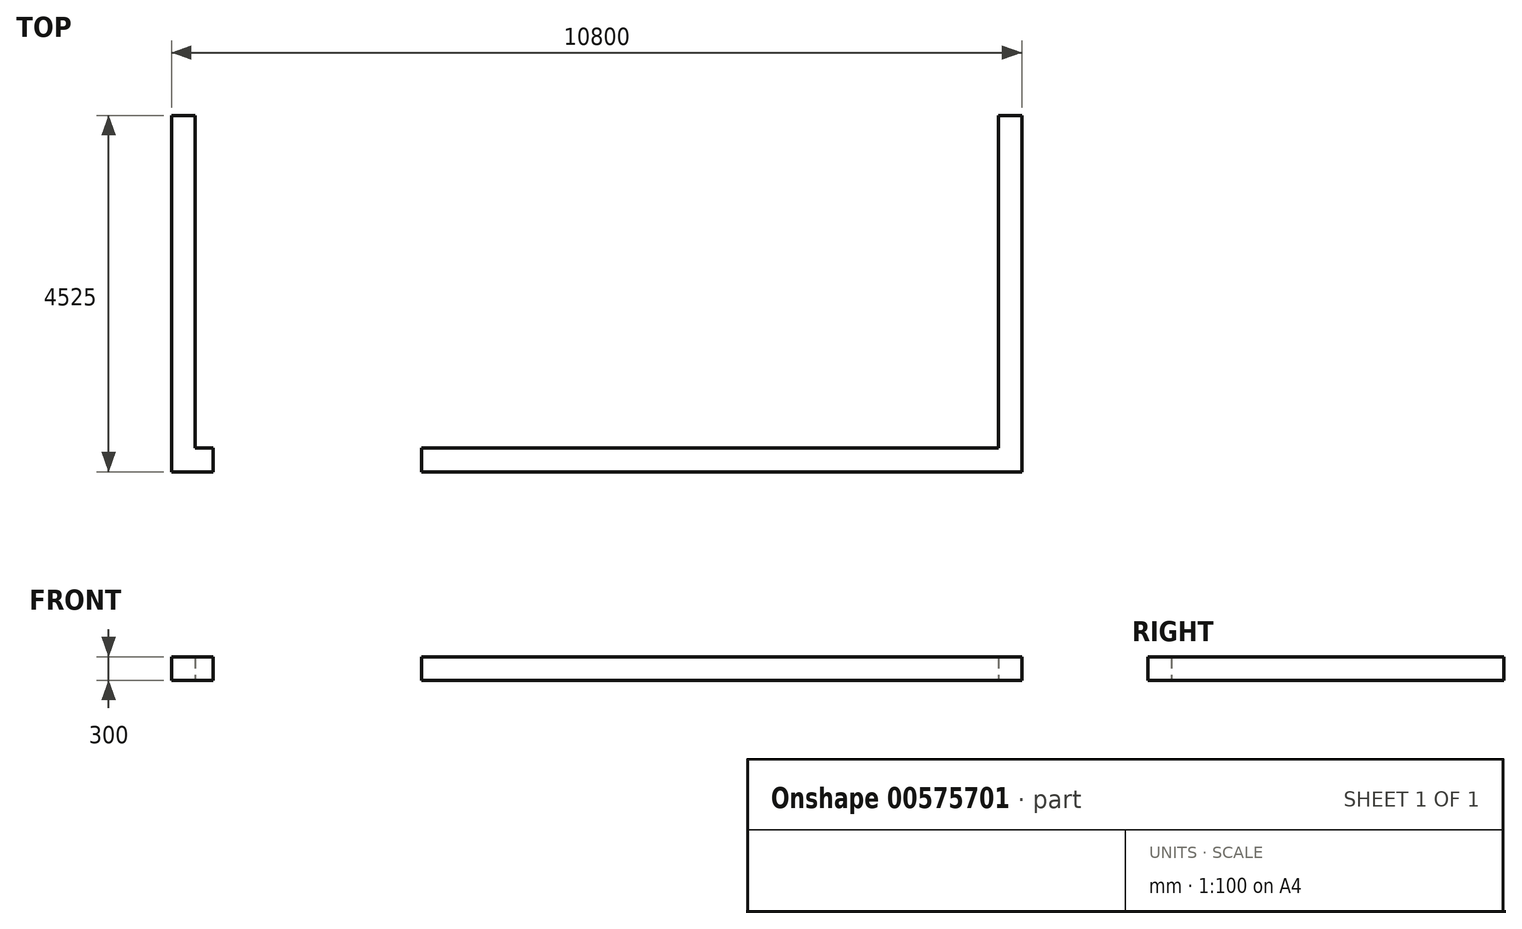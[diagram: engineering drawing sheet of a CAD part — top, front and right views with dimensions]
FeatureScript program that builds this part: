
annotation { "Feature Type Name" : "Feature", "Feature Type Description" : "" }
export const myFeature = defineFeature(function(context is Context, id is Id, definition is map)
    precondition{}
    {
        {
            var Q0;
            Q0=qCreatedBy(makeId("Top.planeOp"),FACE);
            var sketch = newSketch(context, id + "F0", { "sketchPlane" : qUnion([Q0])});
            skLineSegment(sketch, "E0.bottom", {"start": v(0, 0) * mm, "end": v(525, 0) * mm});
            skLineSegment(sketch, "E0.top", {"start": v(0, 4525) * mm, "end": v(300, 4525) * mm});
            skLineSegment(sketch, "E0.left", {"start": v(0, 0) * mm, "end": v(0, 4525) * mm});
            skLineSegment(sketch, "E0.right", {"start": v(10800, 0) * mm, "end": v(10800, 4525) * mm});
            skLineSegment(sketch, "E1.1", {"start": v(300, 300) * mm, "end": v(300, 4225) * mm});
            skLineSegment(sketch, "E1.2", {"start": v(300, 300) * mm, "end": v(525, 300) * mm});
            skLineSegment(sketch, "E1.3", {"start": v(10500, 300) * mm, "end": v(10500, 4225) * mm});
            skLineSegment(sketch, "E2.left", {"start": v(525, 300) * mm, "end": v(525, 0) * mm});
            skLineSegment(sketch, "E2.right", {"start": v(3175, 300) * mm, "end": v(3175, 0) * mm});
            skLineSegment(sketch, "E3.trimOffspring", {"start": v(3175, 300) * mm, "end": v(10500, 300) * mm});
            skLineSegment(sketch, "E4.trimOffspring", {"start": v(3175, 0) * mm, "end": v(10800, 0) * mm});
            skLineSegment(sketch, "E5.left", {"start": v(300, 4225) * mm, "end": v(300, 4525) * mm});
            skLineSegment(sketch, "E5.right", {"start": v(10500, 4225) * mm, "end": v(10500, 4525) * mm});
            skLineSegment(sketch, "E6.trimOffspring", {"start": v(10500, 4525) * mm, "end": v(10800, 4525) * mm});
            skSolve(sketch);
        }
        {
            var Q0;
            Q0=makeQuery(id+"F0.imprint","IMPRINT",FACE,{"disambiguationData":[TD([[makeQuery(id+"F0.imprint","IMPRINT",EDGE,{"derivedFrom":sQuery(id+"F0.wireOp",EDGE,"E0.bottom")}),1.0]])]});
            var Q1;
            Q1=makeQuery(id+"F0.imprint","IMPRINT",FACE,{"disambiguationData":[TD([[makeQuery(id+"F0.imprint","IMPRINT",EDGE,{"derivedFrom":sQuery(id+"F0.wireOp",EDGE,"E0.right")}),1.0]])]});
            extrude(context, id + "F1", {"entities" : qUnion([Q0, Q1]), "depth" : 300 * mm, "offsetDistance" : 25 * mm});
        }
    });
